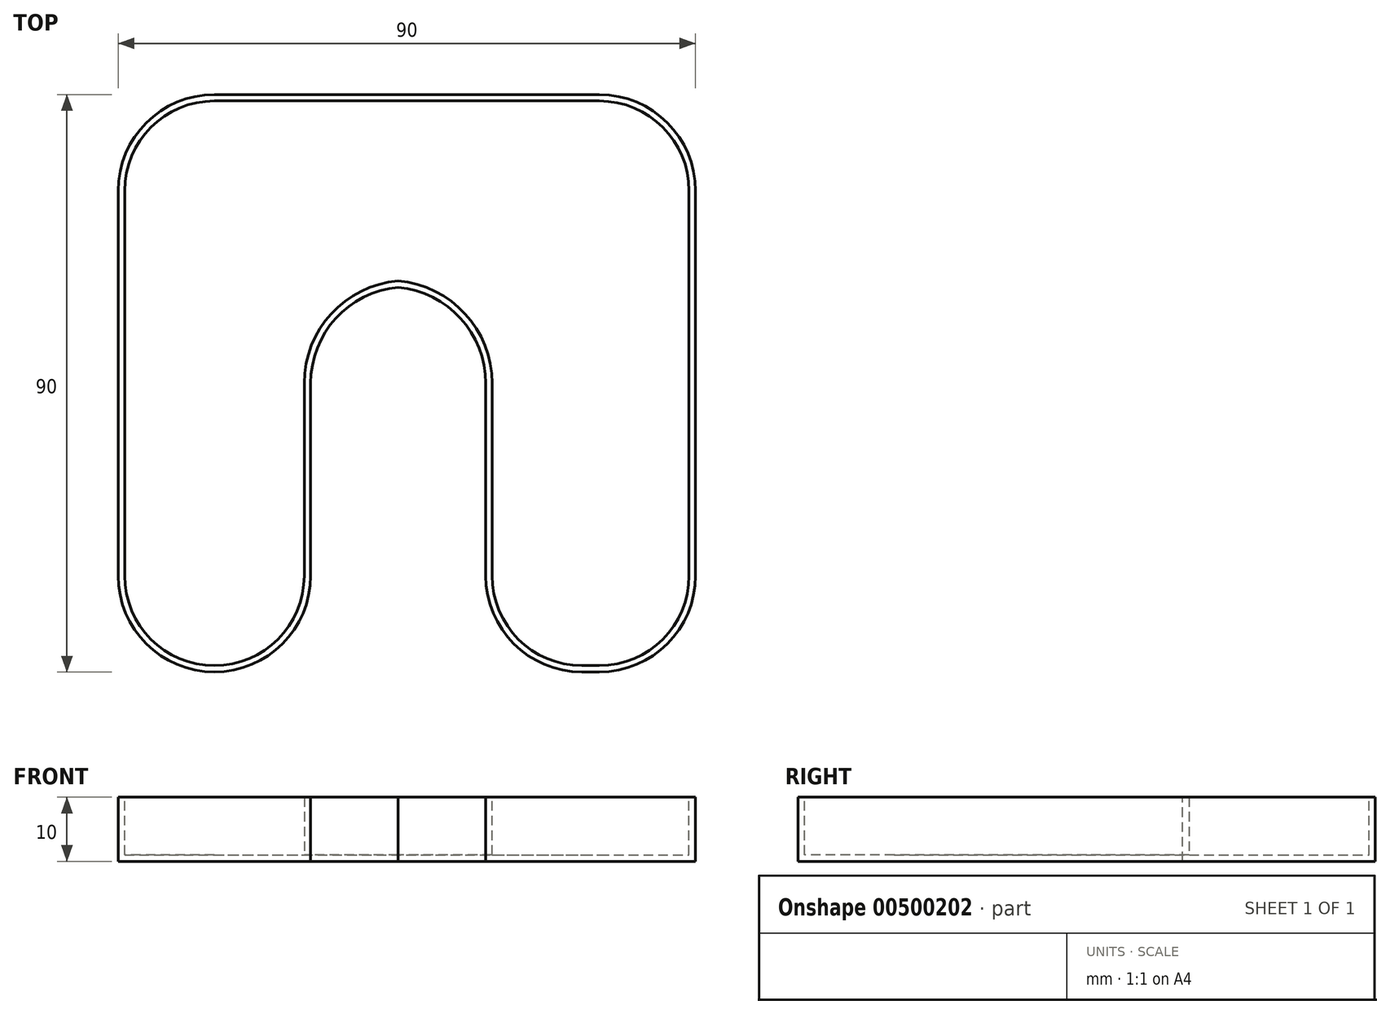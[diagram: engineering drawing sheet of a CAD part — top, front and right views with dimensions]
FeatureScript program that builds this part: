
annotation { "Feature Type Name" : "Feature", "Feature Type Description" : "" }
export const myFeature = defineFeature(function(context is Context, id is Id, definition is map)
    precondition{}
    {
        {
            var Q0;
            Q0=qCreatedBy(makeId("Top.planeOp"),FACE);
            var sketch = newSketch(context, id + "F0", { "sketchPlane" : qUnion([Q0])});
            skLineSegment(sketch, "E0.bottom", {"start": v(0, 0) * mm, "end": v(30, 0) * mm});
            skLineSegment(sketch, "E0.top", {"start": v(0, 90) * mm, "end": v(90, 90) * mm});
            skLineSegment(sketch, "E0.left", {"start": v(0, 0) * mm, "end": v(0, 90) * mm});
            skLineSegment(sketch, "E0.right", {"start": v(90, 0) * mm, "end": v(90, 90) * mm});
            skLineSegment(sketch, "E1", {"start": v(57.3, 60) * mm, "end": v(57.3, 0) * mm});
            skLineSegment(sketch, "E2.trimOffspring", {"start": v(30, 60) * mm, "end": v(30, 0) * mm});
            skLineSegment(sketch, "E3.trimOffspring", {"start": v(57.3, 0) * mm, "end": v(90, 0) * mm});
            skLineSegment(sketch, "E4.trimOffspring", {"start": v(30, 60) * mm, "end": v(57.3, 60) * mm});
            skSolve(sketch);
        }
        {
            var Q0;
            Q0 = qSketchRegion(id + "F0", true);
            var Q1;
            Q1=makeQuery(id+"F0.imprint","IMPRINT",FACE,{"disambiguationData":[TD([[makeQuery(id+"F0.imprint","IMPRINT",EDGE,{"derivedFrom":sQuery(id+"F0.wireOp",EDGE,"E0.bottom")}),1.0]])]});
            extrude(context, id + "F1", {"entities" : qUnion([Q0, Q1]), "depth" : 10 * mm});
        }
        {
            var Q0;
            Q0=makeQuery(id+"F1.opExtrude","SWEPT_EDGE",EDGE,{"disambiguationData":[OSD([sQuery(id+"F0.wireOp",EDGE,"E0.top"),sQuery(id+"F0.wireOp",EDGE,"E0.right")])]});
            var Q1;
            Q1=makeQuery(id+"F1.opExtrude","SWEPT_EDGE",EDGE,{"disambiguationData":[OSD([sQuery(id+"F0.wireOp",EDGE,"E0.right"),sQuery(id+"F0.wireOp",EDGE,"E3.trimOffspring")])]});
            var Q2;
            Q2=makeQuery(id+"F1.opExtrude","SWEPT_EDGE",EDGE,{"disambiguationData":[OSD([sQuery(id+"F0.wireOp",EDGE,"E0.bottom"),sQuery(id+"F0.wireOp",EDGE,"E2.trimOffspring")])]});
            var Q3;
            Q3=makeQuery(id+"F1.opExtrude","SWEPT_EDGE",EDGE,{"disambiguationData":[OSD([sQuery(id+"F0.wireOp",EDGE,"E1"),sQuery(id+"F0.wireOp",EDGE,"E3.trimOffspring")])]});
            var Q4;
            Q4=makeQuery(id+"F1.opExtrude","SWEPT_EDGE",EDGE,{"disambiguationData":[OSD([sQuery(id+"F0.wireOp",EDGE,"E1"),sQuery(id+"F0.wireOp",EDGE,"E4.trimOffspring")])]});
            var Q5;
            Q5=makeQuery(id+"F1.opExtrude","SWEPT_EDGE",EDGE,{"disambiguationData":[OSD([sQuery(id+"F0.wireOp",EDGE,"E0.bottom"),sQuery(id+"F0.wireOp",EDGE,"E0.left")])]});
            var Q6;
            Q6=makeQuery(id+"F1.opExtrude","SWEPT_EDGE",EDGE,{"disambiguationData":[OSD([sQuery(id+"F0.wireOp",EDGE,"E0.top"),sQuery(id+"F0.wireOp",EDGE,"E0.left")])]});
            var Q7;
            Q7=makeQuery(id+"F1.opExtrude","SWEPT_EDGE",EDGE,{"disambiguationData":[OSD([sQuery(id+"F0.wireOp",EDGE,"E2.trimOffspring"),sQuery(id+"F0.wireOp",EDGE,"E4.trimOffspring")])]});
            fillet(context, id + "F2", {"entities" : qUnion([Q0, Q1, Q2, Q3, Q4, Q5, Q6, Q7]), "radius" : 15 * mm, "tangentPropagation" : true, "allowEdgeOverflow" : false});
        }
        {
            var Q0;
            Q0=makeQuery(id+"F1.opExtrude","CAP_FACE",FACE,{"disambiguationData":[OSD([sQuery(id+"F0.wireOp",EDGE,"E0.bottom"),sQuery(id+"F0.wireOp",EDGE,"E0.top"),sQuery(id+"F0.wireOp",EDGE,"E0.left"),sQuery(id+"F0.wireOp",EDGE,"E0.right"),sQuery(id+"F0.wireOp",EDGE,"E1"),sQuery(id+"F0.wireOp",EDGE,"E2.trimOffspring"),sQuery(id+"F0.wireOp",EDGE,"E3.trimOffspring"),sQuery(id+"F0.wireOp",EDGE,"E4.trimOffspring")])],"isStart":false});
            shell(context, id + "F3", {"entities" : qUnion([Q0]), "thickness" : 1 * mm});
        }
    });
